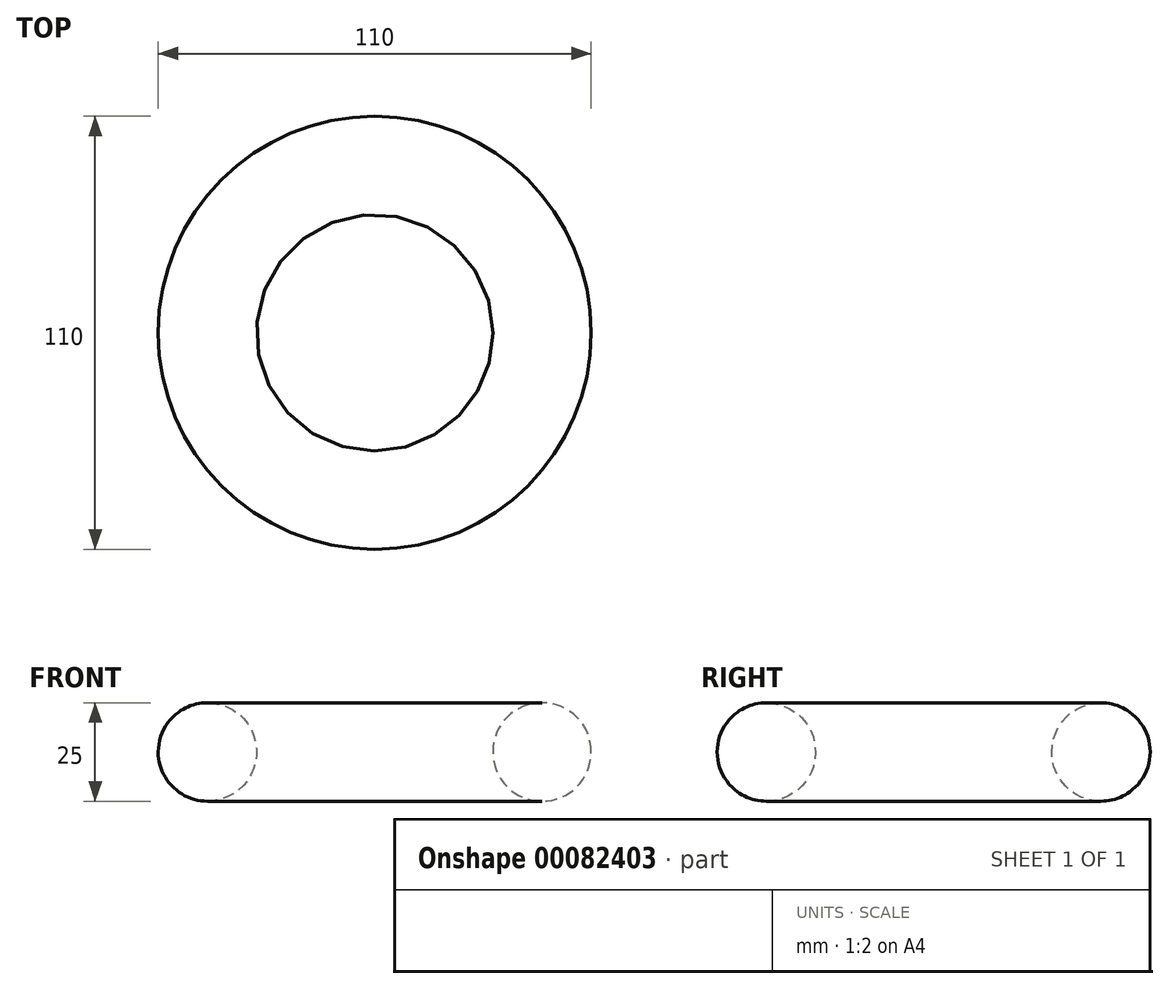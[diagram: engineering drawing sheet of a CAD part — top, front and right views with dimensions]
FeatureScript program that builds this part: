
annotation { "Feature Type Name" : "Feature", "Feature Type Description" : "" }
export const myFeature = defineFeature(function(context is Context, id is Id, definition is map)
    precondition{}
    {
        {
            var Q0;
            Q0=qCreatedBy(makeId("Front.planeOp"),FACE);
            var sketch = newSketch(context, id + "F0", { "sketchPlane" : qUnion([Q0])});
            skCircle(sketch, "E0", {"center": v(-19.04, 0) * mm, "radius": 12.5 * mm});
            skLineSegment(sketch, "E1", {"start": v(-6.54, 0) * mm, "end": v(23.46, 0) * mm});
            skLineSegment(sketch, "E2", {"start": v(23.46, 42.39) * mm, "end": v(23.46, -55.15) * mm});
            skSolve(sketch);
        }
        {
            var Q0;
            Q0=makeQuery(id+"F0.imprint","IMPRINT",FACE,{"disambiguationData":[TD([[makeQuery(id+"F0.imprint","IMPRINT",EDGE,{"derivedFrom":sQuery(id+"F0.wireOp",EDGE,"E0")}),1.0]])]});
            var Q1;
            Q1=sQuery(id+"F0.wireOp",EDGE,"E2");
            revolve(context, id + "F1", {"entities" : qUnion([Q0]), "axis" : qUnion([Q1]), "revolveType" : RevolveType.FULL});
        }
    });
